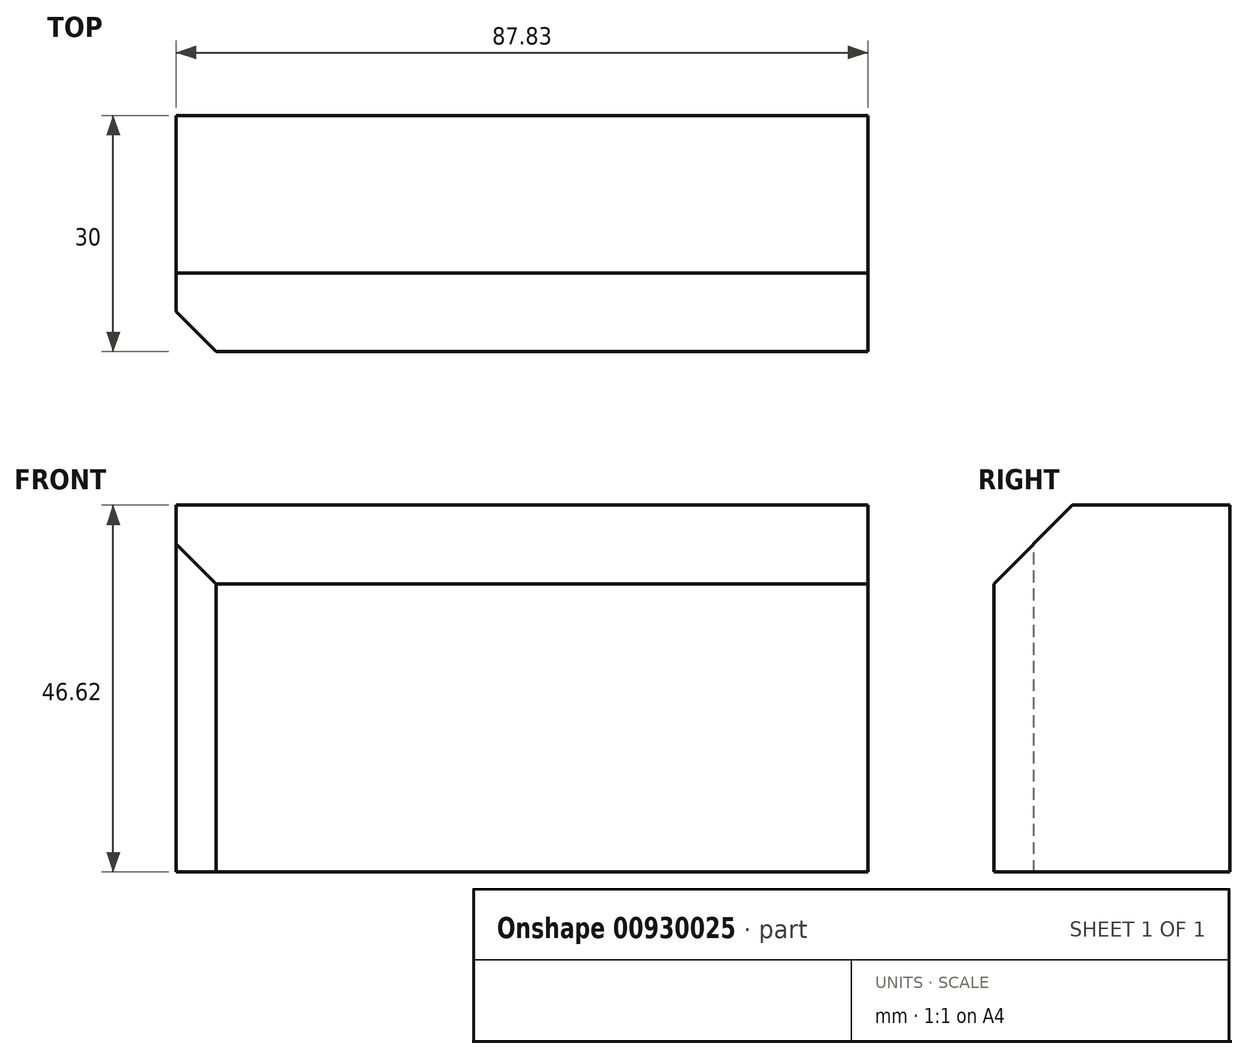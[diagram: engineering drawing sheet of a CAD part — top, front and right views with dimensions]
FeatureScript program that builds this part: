
annotation { "Feature Type Name" : "Feature", "Feature Type Description" : "" }
export const myFeature = defineFeature(function(context is Context, id is Id, definition is map)
    precondition{}
    {
        {
            var Q0;
            Q0=qCreatedBy(makeId("Front.planeOp"),FACE);
            var sketch = newSketch(context, id + "F0", { "sketchPlane" : qUnion([Q0])});
            skLineSegment(sketch, "E0.bottom", {"start": v(-43.46, 26.92) * mm, "end": v(44.37, 26.92) * mm});
            skLineSegment(sketch, "E0.top", {"start": v(-43.46, -19.7) * mm, "end": v(44.37, -19.7) * mm});
            skLineSegment(sketch, "E0.left", {"start": v(-43.46, 26.92) * mm, "end": v(-43.46, -19.7) * mm});
            skLineSegment(sketch, "E0.right", {"start": v(44.37, 26.92) * mm, "end": v(44.37, -19.7) * mm});
            skSolve(sketch);
        }
        {
            var Q0;
            Q0 = qSketchRegion(id + "F0", true);
            extrude(context, id + "F1", {"entities" : qUnion([Q0]), "depth" : 30 * mm, "offsetDistance" : 25.4 * mm});
        }
        {
            var Q0;
            Q0=makeQuery(id+"F1.opExtrude","CAP_EDGE",EDGE,{"disambiguationData":[OSD([sQuery(id+"F0.wireOp",EDGE,"E0.left")])],"isStart":false});
            chamfer(context, id + "F2", {"entities" : qUnion([Q0]), "width" : 5.08 * mm, "tangentPropagation" : true});
        }
        {
            var Q0;
            Q0=makeQuery(id+"F1.opExtrude","CAP_EDGE",EDGE,{"disambiguationData":[OSD([sQuery(id+"F0.wireOp",EDGE,"E0.bottom")])],"isStart":false});
            chamfer(context, id + "F3", {"entities" : qUnion([Q0]), "width" : 10 * mm, "tangentPropagation" : true});
        }
    });
